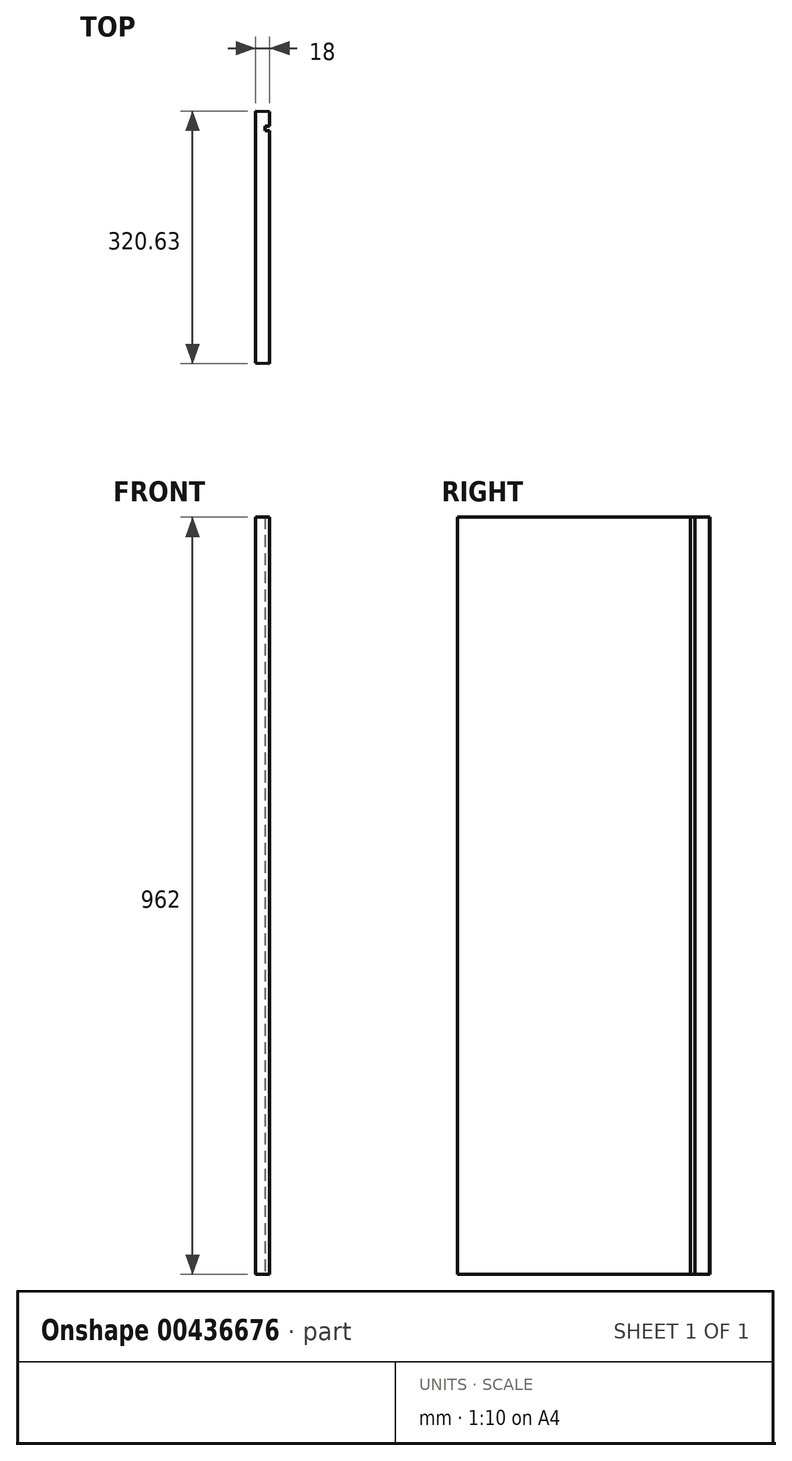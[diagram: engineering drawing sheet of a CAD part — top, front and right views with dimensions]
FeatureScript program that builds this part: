
annotation { "Feature Type Name" : "Feature", "Feature Type Description" : "" }
export const myFeature = defineFeature(function(context is Context, id is Id, definition is map)
    precondition{}
    {
        {
            var Q0;
            Q0=qCreatedBy(makeId("Top.planeOp"),FACE);
            var sketch = newSketch(context, id + "F0", { "sketchPlane" : qUnion([Q0])});
            skLineSegment(sketch, "E0.left", {"start": v(-15.06, 132.16) * mm, "end": v(-15.06, -187.84) * mm});
            skLineSegment(sketch, "E0.right", {"start": v(-33.06, 132.79) * mm, "end": v(-33.06, -187.21) * mm});
            skPoint(sketch, "E0.middle", {"position": v(0, 0) * mm});
            skLineSegment(sketch, "E1", {"start": v(-15.06, -187.84) * mm, "end": v(-33.06, -187.21) * mm});
            skLineSegment(sketch, "E2", {"start": v(-15.06, 132.16) * mm, "end": v(-33.06, 132.79) * mm});
            skSolve(sketch);
        }
        {
            var Q0;
            Q0=qSketchRegion(id+"F0",true);
            extrude(context, id + "F1", {"entities" : qUnion([Q0]), "depth" : 962 * mm});
        }
        {
            var Q0;
            Q0=makeQuery(id+"F1.opExtrude","SWEPT_FACE",FACE,{"disambiguationData":[OSD([sQuery(id+"F0.wireOp",EDGE,"E0.left")])]});
            var sketch = newSketch(context, id + "F2", { "sketchPlane" : qUnion([Q0])});
            skLineSegment(sketch, "E3.bottom", {"start": v(107.79, 962) * mm, "end": v(113.79, 962) * mm});
            skLineSegment(sketch, "E3.top", {"start": v(107.79, 0) * mm, "end": v(113.79, 0) * mm});
            skLineSegment(sketch, "E3.left", {"start": v(107.79, 962) * mm, "end": v(107.79, 0) * mm});
            skLineSegment(sketch, "E3.right", {"start": v(113.79, 962) * mm, "end": v(113.79, 0) * mm});
            skSolve(sketch);
        }
        {
            var Q0;
            Q0=qSketchRegion(id+"F2",true);
            extrude(context, id + "F3", {"entities" : qUnion([Q0]), "operationType" : NewBodyOperationType.REMOVE, "oppositeDirection" : true, "depth" : 6 * mm});
        }
    });
